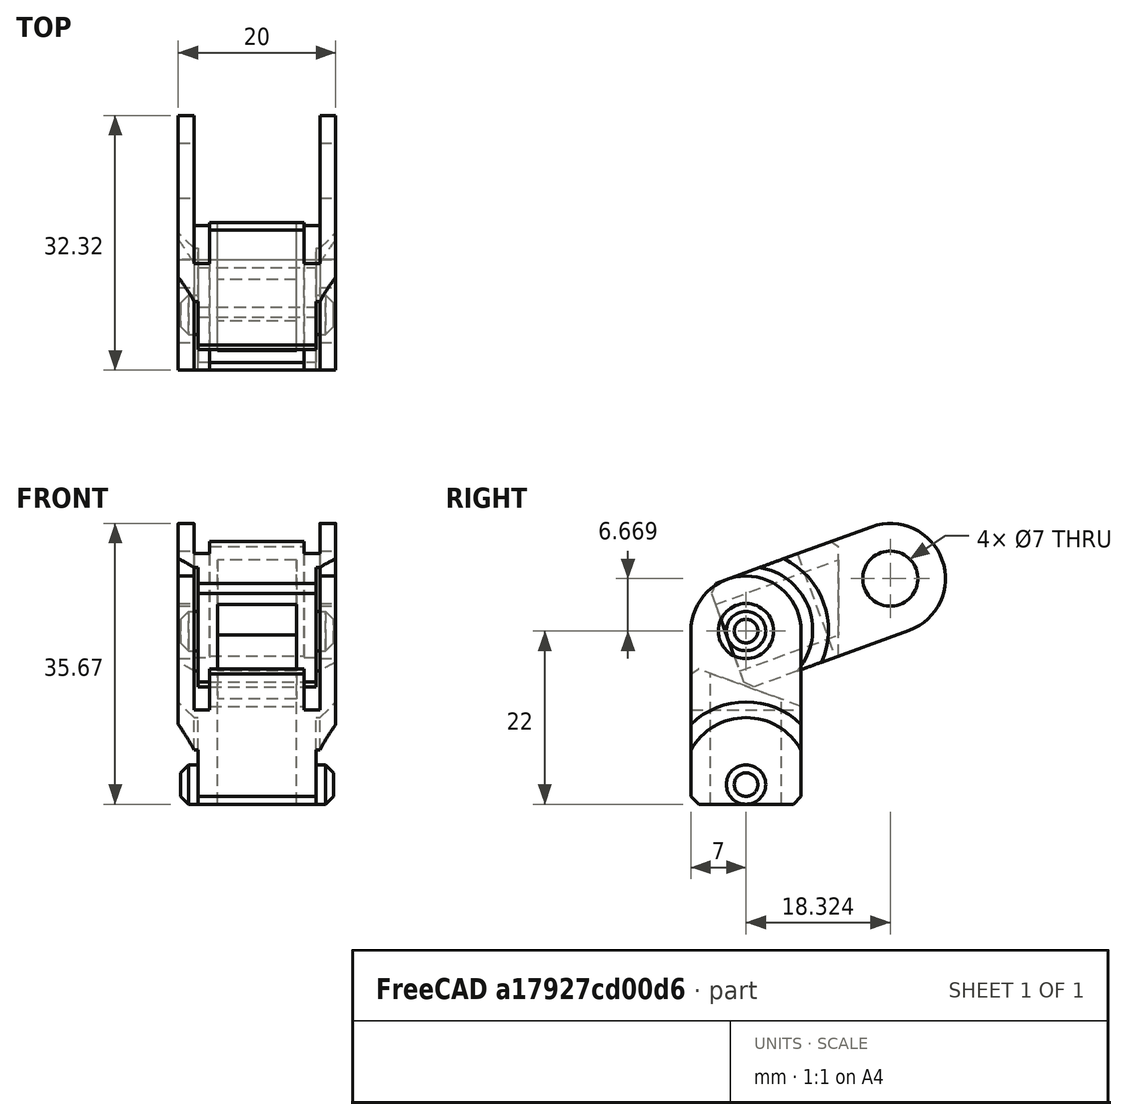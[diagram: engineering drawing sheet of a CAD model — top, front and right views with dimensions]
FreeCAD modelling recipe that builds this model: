
FCSTD DOCUMENT  (FreeCAD 0.14R3692 (Git))
Label: new-cable-chain-2
License: CC-BY 3.0
LicenseURL: http://creativecommons.org/licenses/by/3.0/
objects: Part::Cut×8, Part::Chamfer×8, Part::Box×6, Part::Cylinder×5, Part::Fuse×2
note: 29 computed .brp shape members not serialized (recipe doc carries the construction recipe); baked Part::Feature solids carry a one-line shape summary decoded from their .brp

FEATURE [Part::Cylinder] Cylinder
  Angle = 360
  Height = 19.4
  Placement = pos=(0.3,6,6.5) rot=(0,1,0;1.5708rad)
  Radius = 2.5
FEATURE [Part::Box] Box  label="Cube"
  Height = 25
  Length = 20
  Placement = pos=(0,-1,0) rot=(0,0,1;0rad)
  Width = 14
FEATURE [Part::Cylinder] Cylinder001
  Angle = 360
  Height = 20
  Placement = pos=(0,6,25) rot=(0,1,0;1.5708rad)
  Radius = 7
FEATURE [Part::Box] Box001  label="Cube001"
  Height = 20
  Length = 2
  Placement = pos=(2,-1,15) rot=(0,0,1;0rad)
  Width = 15
FEATURE [Part::Box] Box002  label="Cube002"
  Height = 20
  Length = 2
  Placement = pos=(16,-1,15) rot=(0,0,1;0rad)
  Width = 15
FEATURE [Part::Cylinder] Cylinder002
  Angle = 360
  Height = 25
  Placement = pos=(-2,6,25) rot=(0,1,0;1.5708rad)
  Radius = 3.5
FEATURE [Part::Box] Box003  label="Cube003"
  Height = 20
  Length = 15
  Placement = pos=(2.5,-5,22) rot=(-1,0,0;0.349066rad)
  Width = 20
FEATURE [Part::Cylinder] Cylinder003
  Angle = 360
  Height = 5
  Placement = pos=(-2.5,6,6) rot=(0,1,0;1.5708rad)
  Radius = 8
FEATURE [Part::Cylinder] Cylinder004
  Angle = 360
  Height = 5
  Placement = pos=(17.5,6,6) rot=(0,1,0;1.5708rad)
  Radius = 8
FEATURE [Part::Box] Box006  label="Cube006"
  Height = 30
  Length = 10
  Placement = pos=(5,1.5,-1) rot=(0,0,1;0rad)
  Width = 9
FEATURE [Part::Box] Box007  label="Cube007"
  Height = 10
  Length = 30
  Placement = pos=(-1,-2,-7) rot=(0,0,1;0rad)
  Width = 16
FEATURE [Part::Fuse] Fusion
  Base = -> Box
  Tool = -> Cylinder001
FEATURE [Part::Cut] Cut
  Base = -> Fusion
  Tool = -> Box007
FEATURE [Part::Cut] Cut001
  Base = -> Cut
  Tool = -> Box002
FEATURE [Part::Cut] Cut002
  Base = -> Cut001
  Tool = -> Box001
FEATURE [Part::Cut] Cut003
  Base = -> Cut002
  Tool = -> Box003
FEATURE [Part::Cut] Cut004
  Base = -> Cut003
  Tool = -> Cylinder002
FEATURE [Part::Cut] Cut005
  Base = -> Cut004
  Tool = -> Cylinder004
FEATURE [Part::Cut] Cut006
  Base = -> Cut005
  Tool = -> Cylinder003
FEATURE [Part::Fuse] Fusion001
  Base = -> Cylinder
  Tool = -> Cut006
FEATURE [Part::Cut] Cut007
  Base = -> Fusion001
  Tool = -> Box006
FEATURE [Part::Chamfer] Chamfer
  Base = -> Cut007
  Edges = 1 edges r=1: [Edge22]
FEATURE [Part::Chamfer] Chamfer001
  Base = -> Chamfer
  Edges = 1 edges r=1: [Edge46]
FEATURE [Part::Chamfer] Chamfer002
  Base = -> Chamfer001
  Edges = 1 edges r=1: [Edge22]
FEATURE [Part::Chamfer] Chamfer003
  Base = -> Chamfer002
  Edges = 1 edges r=2: [Edge49]
FEATURE [Part::Chamfer] Chamfer004
  Base = -> Chamfer003
  Edges = 1 edges r=2: [Edge53]
  Placement = pos=(0,-6,-5.5) rot=(0,0,1;0rad)
FEATURE [Part::Chamfer] Chamfer005
  Base = -> Chamfer004
  Edges = 1 edges r=1: [Edge83]
FEATURE [Part::Chamfer] Chamfer006
  Base = -> Chamfer005
  Edges = 1 edges r=1: [Edge100]
FEATURE [Part::Chamfer] Chamfer007
  Base = -> Chamfer005
  Edges = 1 edges r=1: [Edge100]
  Placement = pos=(0,0,19.5) rot=(-1,0,0;1.22173rad)
